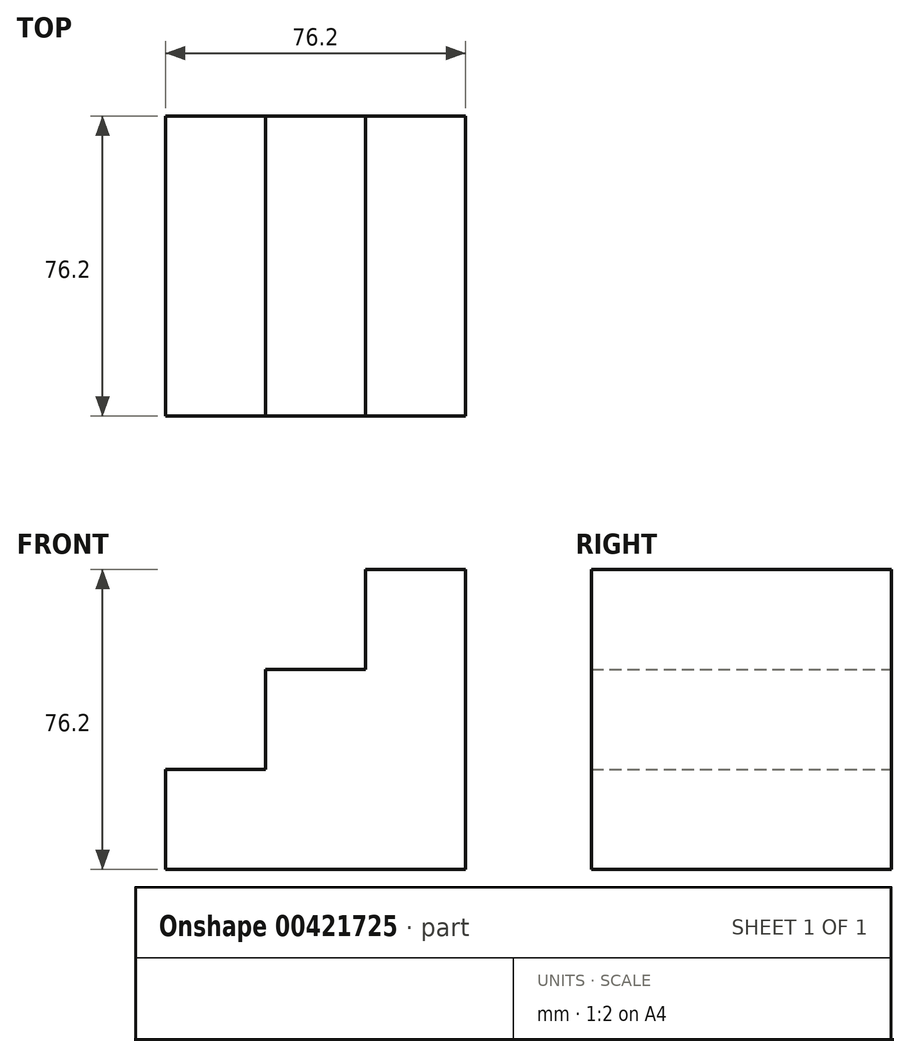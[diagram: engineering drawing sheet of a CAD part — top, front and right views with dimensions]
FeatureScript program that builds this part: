
annotation { "Feature Type Name" : "Feature", "Feature Type Description" : "" }
export const myFeature = defineFeature(function(context is Context, id is Id, definition is map)
    precondition{}
    {
        {
            var Q0;
            Q0=qCreatedBy(makeId("Front.planeOp"),FACE);
            var sketch = newSketch(context, id + "F0", { "sketchPlane" : qUnion([Q0])});
            skLineSegment(sketch, "E0", {"start": v(0, 0) * mm, "end": v(-76.2, 0) * mm});
            skLineSegment(sketch, "E1", {"start": v(0, 0) * mm, "end": v(0, 76.2) * mm});
            skLineSegment(sketch, "E2", {"start": v(0, 76.2) * mm, "end": v(-25.4, 76.2) * mm});
            skLineSegment(sketch, "E3", {"start": v(-25.4, 76.2) * mm, "end": v(-25.4, 50.8) * mm});
            skLineSegment(sketch, "E4", {"start": v(-25.4, 50.8) * mm, "end": v(-50.8, 50.8) * mm});
            skLineSegment(sketch, "E5", {"start": v(-50.8, 50.8) * mm, "end": v(-50.8, 25.4) * mm});
            skLineSegment(sketch, "E6", {"start": v(-50.8, 25.4) * mm, "end": v(-76.2, 25.4) * mm});
            skLineSegment(sketch, "E7", {"start": v(-76.2, 25.4) * mm, "end": v(-76.2, 0) * mm});
            skSolve(sketch);
        }
        {
            var Q0;
            Q0=makeQuery(id+"F0.imprint","IMPRINT",FACE,{"disambiguationData":[TD([[makeQuery(id+"F0.imprint","IMPRINT",EDGE,{"derivedFrom":sQuery(id+"F0.wireOp",EDGE,"E0")}),-1.0]])]});
            extrude(context, id + "F1", {"entities" : qUnion([Q0]), "depth" : 76.2 * mm});
        }
    });
